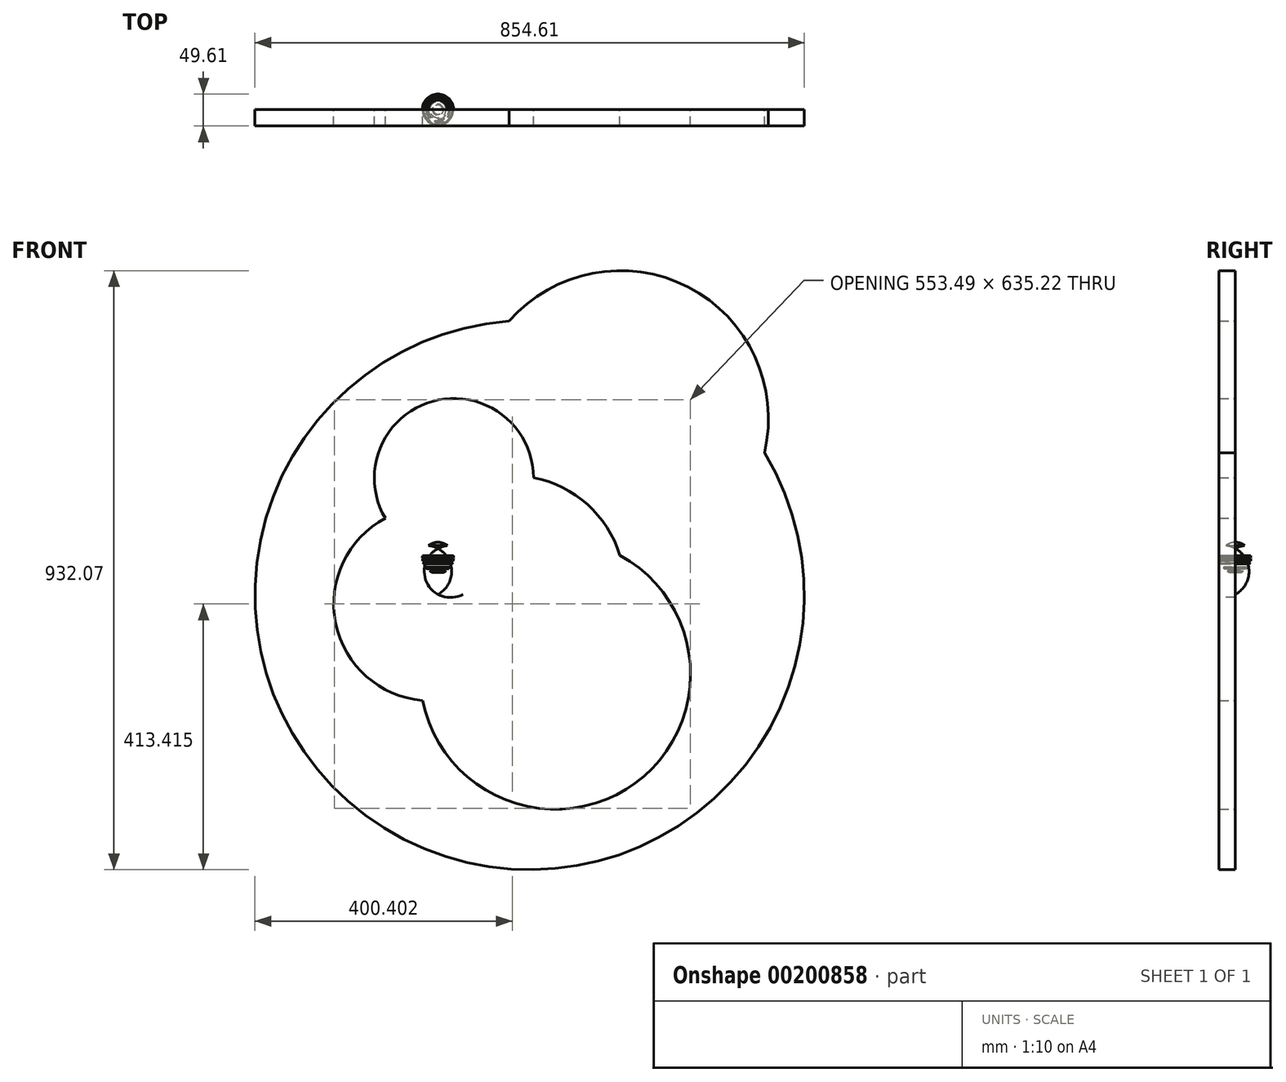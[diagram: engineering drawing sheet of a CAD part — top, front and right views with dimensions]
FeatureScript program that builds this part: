
annotation { "Feature Type Name" : "Feature", "Feature Type Description" : "" }
export const myFeature = defineFeature(function(context is Context, id is Id, definition is map)
    precondition{}
    {
        {
            var Q0;
            Q0=qCreatedBy(makeId("Front.planeOp"),FACE);
            var sketch = newSketch(context, id + "F0", { "sketchPlane" : qUnion([Q0])});
            skArc(sketch, "E0", {"start": v(-44.77, 24.4) * mm, "mid": v(-20.56, 48.6) * mm, "end": v(-44.77, 72.81) * mm});
            skLineSegment(sketch, "E1", {"start": v(-44.77, 72.81) * mm, "end": v(-44.77, 24.4) * mm});
            skCircle(sketch, "E2", {"center": v(-39.84, 9.93) * mm, "radius": 30.66 * mm});
            skCircle(sketch, "E3", {"center": v(-39.84, 9.93) * mm, "radius": 27.21 * mm});
            skCircle(sketch, "E4", {"center": v(-28.94, -9.54) * mm, "radius": 5.98 * mm});
            skCircle(sketch, "E5", {"center": v(-60.35, -4.6) * mm, "radius": 64.12 * mm});
            skCircle(sketch, "E6", {"center": v(-102.92, -10.06) * mm, "radius": 39.7 * mm});
            skCircle(sketch, "E7", {"center": v(-14.28, -26.02) * mm, "radius": 27.78 * mm});
            skCircle(sketch, "E8", {"center": v(20.9, -17.2) * mm, "radius": 51.3 * mm});
            skCircle(sketch, "E9", {"center": v(-52.95, -0.45) * mm, "radius": 54.54 * mm});
            skCircle(sketch, "E10", {"center": v(-110.84, 24.72) * mm, "radius": 70.14 * mm});
            skCircle(sketch, "E11", {"center": v(1.95, 24.98) * mm, "radius": 30.43 * mm});
            skCircle(sketch, "E12", {"center": v(53.6, 25.9) * mm, "radius": 115.8 * mm});
            skCircle(sketch, "E13", {"center": v(-64.64, 14.47) * mm, "radius": 30.7 * mm});
            skCircle(sketch, "E14", {"center": v(-36.6, 30.43) * mm, "radius": 45.04 * mm});
            skCircle(sketch, "E15", {"center": v(-21.8, -4.74) * mm, "radius": 40.18 * mm});
            skCircle(sketch, "E16", {"center": v(-6.62, -41.34) * mm, "radius": 20.23 * mm});
            skCircle(sketch, "E17", {"center": v(-0.26, -20.18) * mm, "radius": 17.77 * mm});
            skCircle(sketch, "E18", {"center": v(-29.6, -8.37) * mm, "radius": 49.19 * mm});
            skCircle(sketch, "E19", {"center": v(-9.6, -40.43) * mm, "radius": 9.62 * mm});
            skCircle(sketch, "E20", {"center": v(-8.05, -51.2) * mm, "radius": 25.48 * mm});
            skCircle(sketch, "E21", {"center": v(8.3, -19.14) * mm, "radius": 29.28 * mm});
            skCircle(sketch, "E22", {"center": v(39.33, 10.58) * mm, "radius": 10.42 * mm});
            skCircle(sketch, "E23", {"center": v(25.7, -2.8) * mm, "radius": 58.3 * mm});
            skCircle(sketch, "E24", {"center": v(-39.2, 4.48) * mm, "radius": 24.44 * mm});
            skCircle(sketch, "E25", {"center": v(-25.44, 27.45) * mm, "radius": 40.56 * mm});
            skCircle(sketch, "E26", {"center": v(4.28, -7.2) * mm, "radius": 30.32 * mm});
            skCircle(sketch, "E27", {"center": v(65.94, -11.49) * mm, "radius": 152.72 * mm});
            skCircle(sketch, "E28", {"center": v(-91.5, -13.82) * mm, "radius": 2.24 * mm});
            skCircle(sketch, "E29", {"center": v(-84.75, -3.57) * mm, "radius": 19.23 * mm});
            skCircle(sketch, "E30", {"center": v(-35.95, 10.7) * mm, "radius": 29.17 * mm});
            skCircle(sketch, "E31", {"center": v(35.7, -2.53) * mm, "radius": 11.37 * mm});
            skCircle(sketch, "E32", {"center": v(21.55, 17.59) * mm, "radius": 51.66 * mm});
            skCircle(sketch, "E33", {"center": v(-27.77, 60.8) * mm, "radius": 55.94 * mm});
            skCircle(sketch, "E34", {"center": v(-43.74, 0.32) * mm, "radius": 86.95 * mm});
            skCircle(sketch, "E35", {"center": v(39.59, 57.69) * mm, "radius": 14.36 * mm});
            skCircle(sketch, "E36", {"center": v(36.34, 44.97) * mm, "radius": 14.33 * mm});
            skCircle(sketch, "E37", {"center": v(21.8, 40.3) * mm, "radius": 44.26 * mm});
            skCircle(sketch, "E38", {"center": v(17, -3.7) * mm, "radius": 33.4 * mm});
            skCircle(sketch, "E39", {"center": v(13.95, -9.5) * mm, "radius": 6.42 * mm});
            skCircle(sketch, "E40", {"center": v(33.7, 25.61) * mm, "radius": 47.19 * mm});
            skCircle(sketch, "E41", {"center": v(29.02, 78.07) * mm, "radius": 11.44 * mm});
            skCircle(sketch, "E42", {"center": v(21.63, 40.2) * mm, "radius": 36.95 * mm});
            skCircle(sketch, "E43", {"center": v(-9.28, 68.75) * mm, "radius": 90.82 * mm});
            skCircle(sketch, "E44", {"center": v(-44.38, -15.17) * mm, "radius": 15.37 * mm});
            skCircle(sketch, "E45", {"center": v(-33.23, -7.76) * mm, "radius": 22.5 * mm});
            skCircle(sketch, "E46", {"center": v(-80.24, -4.02) * mm, "radius": 60.86 * mm});
            skCircle(sketch, "E47", {"center": v(-20.52, -61.14) * mm, "radius": 41.8 * mm});
            skCircle(sketch, "E48", {"center": v(-56.25, -23.1) * mm, "radius": 150.62 * mm});
            skCircle(sketch, "E49", {"center": v(24.7, 31.64) * mm, "radius": 102.56 * mm});
            skCircle(sketch, "E50", {"center": v(-20, 172.86) * mm, "radius": 123.78 * mm});
            skCircle(sketch, "E51", {"center": v(83.24, 90.1) * mm, "radius": 74.02 * mm});
            skCircle(sketch, "E52", {"center": v(69.78, 0.39) * mm, "radius": 176.45 * mm});
            skCircle(sketch, "E53", {"center": v(137.74, -132.2) * mm, "radius": 210.45 * mm});
            skCircle(sketch, "E54", {"center": v(34.34, 39.32) * mm, "radius": 43.26 * mm});
            skCircle(sketch, "E55", {"center": v(74.8, 20.54) * mm, "radius": 24.42 * mm});
            skCircle(sketch, "E56", {"center": v(97.86, -9.3) * mm, "radius": 427.3 * mm});
            skCircle(sketch, "E57", {"center": v(239.1, 265.19) * mm, "radius": 230.27 * mm});
            skSolve(sketch);
        }
        {
            var Q0;
            Q0=makeQuery(id+"F0.imprint","IMPRINT",FACE,{"disambiguationData":[TD([[makeQuery(id+"F0.imprint","IMPRINT",EDGE,{"derivedFrom":sQuery(id+"F0.wireOp",EDGE,"E0")}),1.0]])]});
            var Q1;
            Q1=sQuery(id+"F0.wireOp",EDGE,"E1");
            revolve(context, id + "F1", {"entities" : qUnion([Q0]), "axis" : qUnion([Q1]), "revolveType" : RevolveType.FULL});
        }
        {
            var Q0;
            Q0 = qSketchRegion(id + "F0", true);
            extrude(context, id + "F2", {"entities" : qUnion([Q0]), "depth" : 25.4 * mm});
        }
    });
